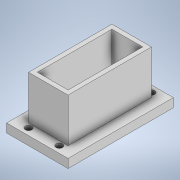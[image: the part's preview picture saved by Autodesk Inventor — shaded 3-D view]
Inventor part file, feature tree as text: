
AUTODESK INVENTOR PART (.ipt)
format: ipt  version: 2022 (Build 260153000, 153)  size: 133,632 bytes
history: native  units: mm
features: extrude x3, sketch x3
ambient origin geometry x8: Origin, YZ Plane, XZ Plane, XY Plane, X Axis, Y Axis, Z Axis, Center Point
bodies: Solid1 (feature_tree)
feature tree (6):
  extrude  "Extrusion1"  Depth=12.0mm
  extrude  "Extrusion2"  Depth=1.0mm TaperAngle=0.0deg
  extrude  "Extrusion3"  Depth=5.0mm TaperAngle=0.0deg
  sketch  "Sketch1"  dims[d0=7.0mm d1=12.0mm]
  sketch  "Sketch2"  dims[d2=1.75mm d3=1.0mm d4=0.0mm]
  sketch  "Sketch3"  dims[d5=0.5mm d6=5.0mm d7=0.0mm d8=0.75mm d9=0.75mm d10=1.75mm d11=20.0mm d13=3.5mm d14=20.0mm d16=10.5mm d19=5.0mm d20=0.0mm d21=0.5mm d22=0.872665mm d23=0.5mm d24=0.872665mm]
